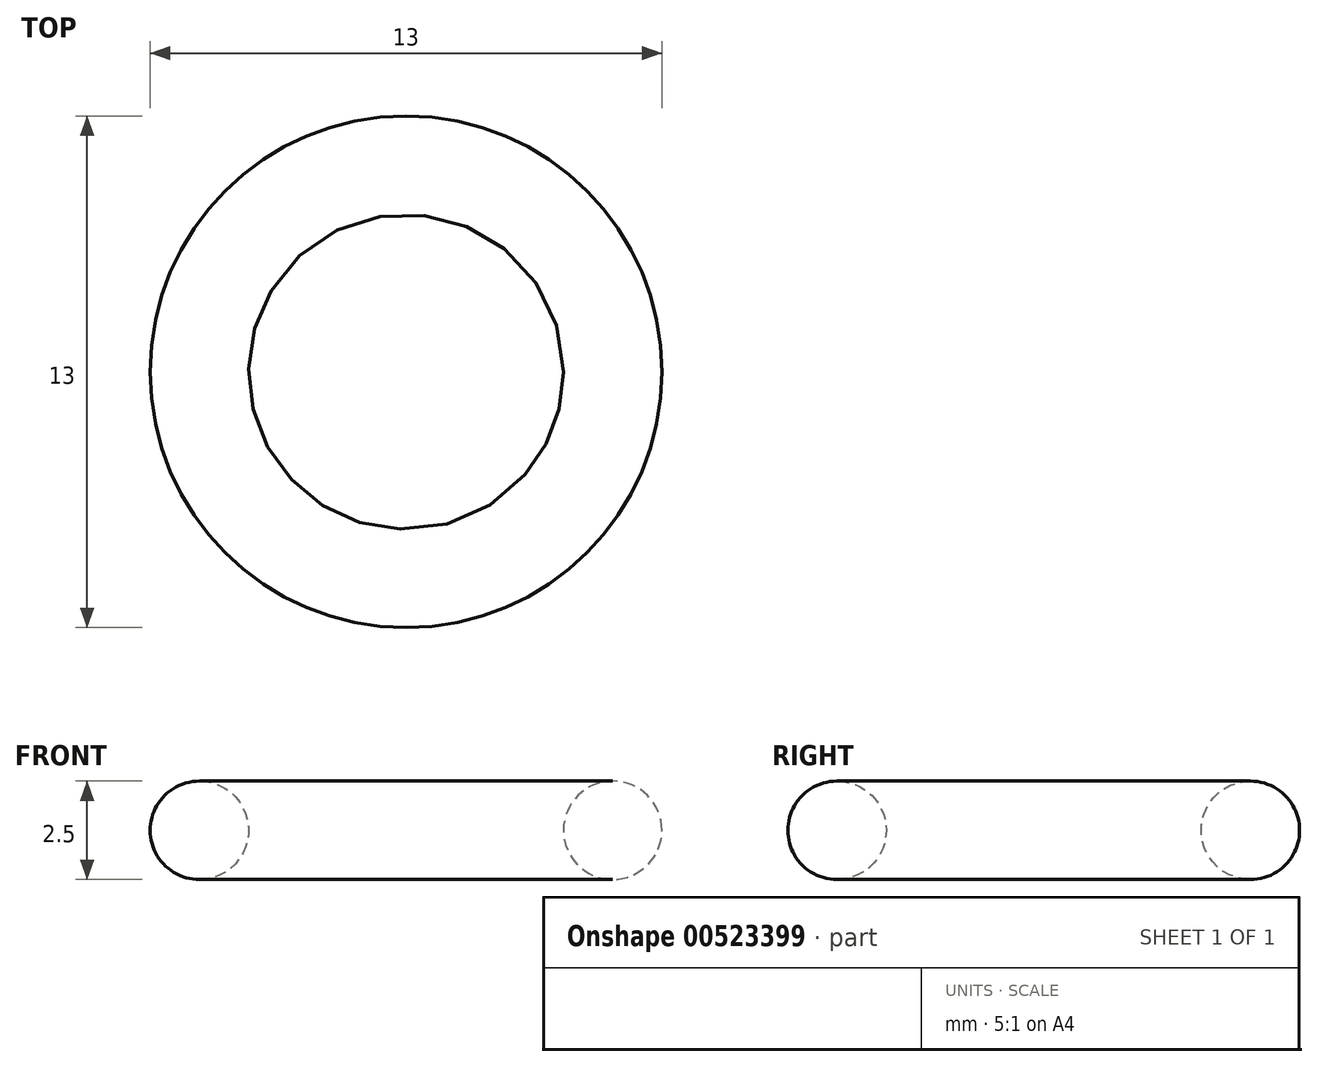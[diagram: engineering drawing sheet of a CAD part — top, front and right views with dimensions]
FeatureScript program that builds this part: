
annotation { "Feature Type Name" : "Feature", "Feature Type Description" : "" }
export const myFeature = defineFeature(function(context is Context, id is Id, definition is map)
    precondition{}
    {
        {
            var Q0;
            Q0=qCreatedBy(makeId("Front.planeOp"),FACE);
            var sketch = newSketch(context, id + "F0", { "sketchPlane" : qUnion([Q0])});
            skCircle(sketch, "E0", {"center": v(-5.25, 0) * mm, "radius": 1.25 * mm});
            skLineSegment(sketch, "E1", {"start": v(0, 7.02) * mm, "end": v(0, -6.52) * mm, "construction": true});
            skSolve(sketch);
        }
        {
            var Q0;
            Q0 = qSketchRegion(id + "F0", true);
            var Q1;
            Q1=sQuery(id+"F0.wireOp",EDGE,"E1");
            revolve(context, id + "F1", {"surfaceOperationType" : NewSurfaceOperationType.NEW, "entities" : qUnion([Q0]), "axis" : qUnion([Q1]), "revolveType" : RevolveType.FULL});
        }
    });
